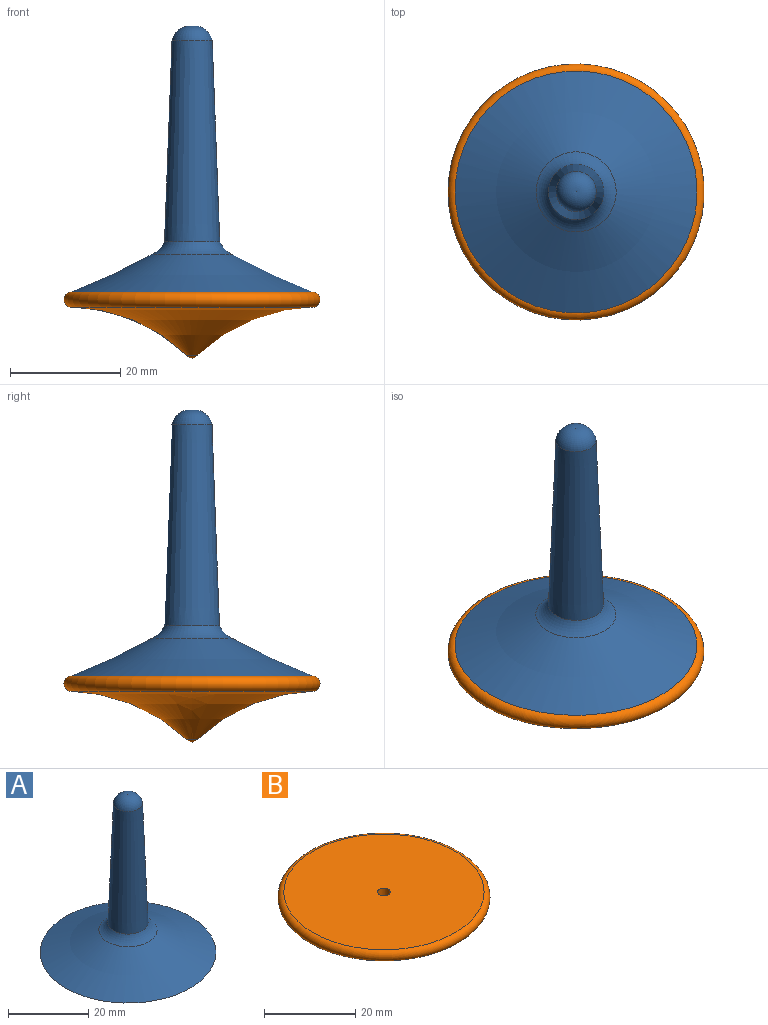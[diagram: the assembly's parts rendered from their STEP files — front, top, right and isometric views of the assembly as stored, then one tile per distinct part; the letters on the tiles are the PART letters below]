
ASSEMBLY  parts=2 mates=1
PART A: 7 faces, bbox 43.9x43.9x56.1 mm
  f0: cylinder r=1.41mm len=6mm, axis (0,0,-1), area 53.2mm2, adj f1,f6
  f1: plane 43.91x43.91mm, normal (0,0,-1), area 1507.9mm2, adj f0,f2
  f2: torus R=63.9mm, axis (0,0,-1), area 1480.5mm2, adj f1,f3
  f3: torus R=9.44mm, axis (0,0,-1), area 123mm2, adj f2,f4
  f4: cone r=5.01mm half-angle=2.1deg, axis (0,0,-1), area 994.5mm2, adj f3,f5
  f5: torus R=0.45mm, axis (0,0,-1), area 67.9mm2, adj f4
  f6: plane 2.82x2.82mm, normal (0,0,-1), area 6.2mm2, adj f0
PART B: 6 faces, bbox 50.3x50.3x12 mm
  f0: torus R=22.92mm, axis (0,0,-1), area 1595.4mm2, adj f1,f5
  f1: torus R=21.87mm, axis (0,0,-1), area 593.1mm2, adj f0,f2
  f2: plane 43.91x43.91mm, normal (0,0,1), area 1507.9mm2, adj f1,f3
  f3: cylinder r=1.41mm len=6mm, axis (0,0,-1), area 53.2mm2, adj f2,f4
  f4: plane 2.82x2.82mm, normal (0,0,1), area 6.2mm2, adj f3
  f5: sphere r=1.18mm, area 3.5mm2, adj f0
PLACE A t=(-18.04,3.21,22.49)mm
PLACE B t=(-18.04,3.21,30.88)mm
MATE parallel B.f3 <-> A.f0  axis (0,0,1) through (-18.04,3.21,34.81)mm
